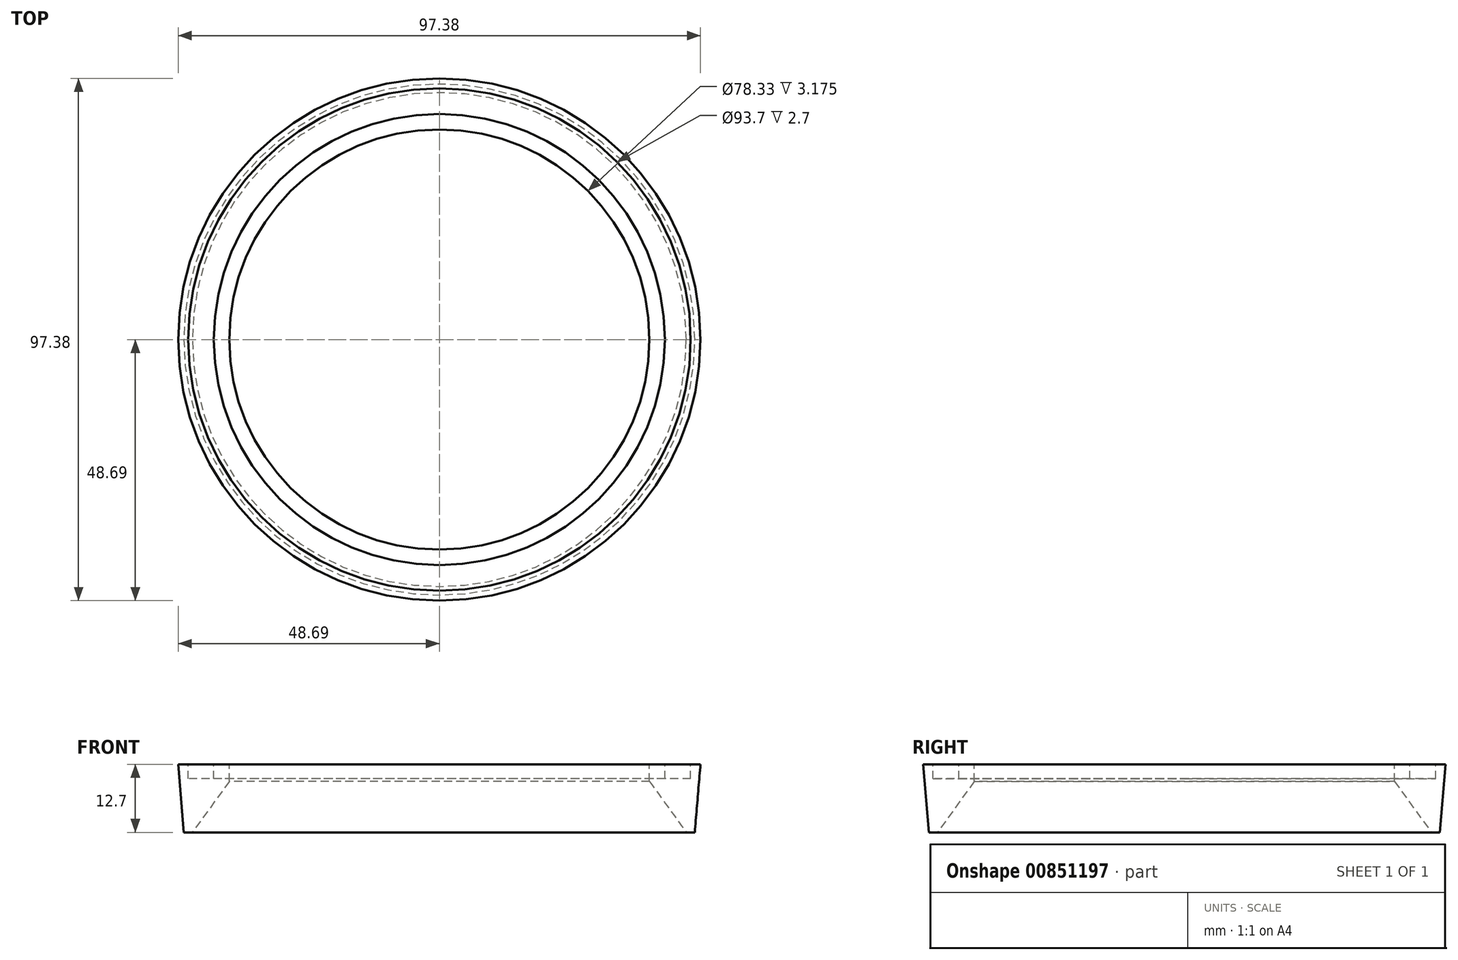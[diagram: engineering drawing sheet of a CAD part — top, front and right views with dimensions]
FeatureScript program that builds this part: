
annotation { "Feature Type Name" : "Feature", "Feature Type Description" : "" }
export const myFeature = defineFeature(function(context is Context, id is Id, definition is map)
    precondition{}
    {
        {
            var Q0;
            Q0=qCreatedBy(makeId("Front.planeOp"),FACE);
            var sketch = newSketch(context, id + "F0", { "sketchPlane" : qUnion([Q0])});
            skLineSegment(sketch, "E0", {"start": v(39.17, 0) * mm, "end": v(39.17, -3.18) * mm});
            skLineSegment(sketch, "E1", {"start": v(39.17, -3.18) * mm, "end": v(46.04, -12.7) * mm});
            skLineSegment(sketch, "E2", {"start": v(46.04, -12.7) * mm, "end": v(47.63, -12.7) * mm});
            skLineSegment(sketch, "E3", {"start": v(47.63, -12.7) * mm, "end": v(48.7, 0) * mm});
            skLineSegment(sketch, "E4", {"start": v(48.7, 0) * mm, "end": v(45.95, 0) * mm});
            skLineSegment(sketch, "E5", {"start": v(39.17, 0) * mm, "end": v(42.95, 0) * mm});
            skArc(sketch, "E6", {"start": v(42.95, 0) * mm, "mid": v(44.45, -1.06) * mm, "end": v(45.95, 0) * mm, "construction": true});
            skLineSegment(sketch, "E7", {"start": v(40.45, -1.06) * mm, "end": v(46, -1.06) * mm, "construction": true});
            skLineSegment(sketch, "E8", {"start": v(0, 15.42) * mm, "end": v(0, -20.5) * mm, "construction": true});
            skLineSegment(sketch, "E9.bottom", {"start": v(42.05, 0) * mm, "end": v(42.95, 0) * mm});
            skLineSegment(sketch, "E9.top", {"start": v(42.05, -2.7) * mm, "end": v(46.85, -2.7) * mm});
            skLineSegment(sketch, "E9.left", {"start": v(42.05, 0) * mm, "end": v(42.05, -2.7) * mm});
            skLineSegment(sketch, "E9.right", {"start": v(46.85, 0) * mm, "end": v(46.85, -2.7) * mm});
            skLineSegment(sketch, "E10.trimOffspring", {"start": v(45.95, 0) * mm, "end": v(46.85, 0) * mm});
            skSolve(sketch);
        }
        {
            var Q0;
            Q0 = qSketchRegion(id + "F0", true);
            var Q1;
            Q1=sQuery(id+"F0.wireOp",EDGE,"E8");
            revolve(context, id + "F1", {"surfaceOperationType" : NewSurfaceOperationType.NEW, "entities" : qUnion([Q0]), "axis" : qUnion([Q1]), "revolveType" : RevolveType.FULL});
        }
    });
